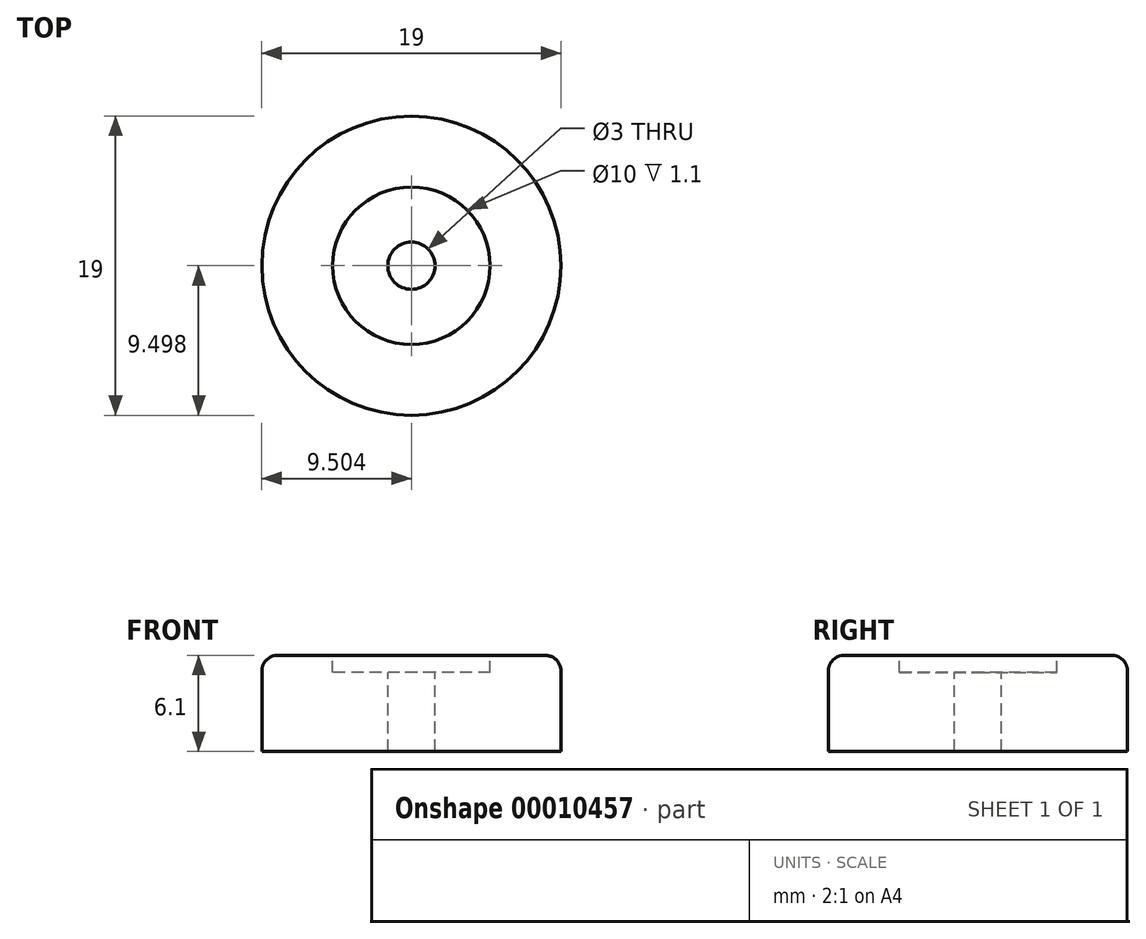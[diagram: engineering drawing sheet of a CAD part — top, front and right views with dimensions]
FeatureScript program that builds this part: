
annotation { "Feature Type Name" : "Feature", "Feature Type Description" : "" }
export const myFeature = defineFeature(function(context is Context, id is Id, definition is map)
    precondition{}
    {
        {
            var Q0;
            Q0=qCreatedBy(makeId("Top.planeOp"),FACE);
            var sketch = newSketch(context, id + "F0", { "sketchPlane" : qUnion([Q0])});
            skCircle(sketch, "E0", {"center": v(-57.53, -50.42) * mm, "radius": 9.5 * mm});
            skSolve(sketch);
        }
        {
            var Q0;
            Q0=makeQuery(id+"F0.imprint","IMPRINT",FACE,{"disambiguationData":[TD([[makeQuery(id+"F0.imprint","IMPRINT",EDGE,{"derivedFrom":sQuery(id+"F0.wireOp",EDGE,"E0")}),1.0]])]});
            extrude(context, id + "F1", {"entities" : qUnion([Q0]), "depth" : 6.1 * mm});
        }
        {
            var Q0;
            Q0=makeQuery(id+"F1.opExtrude","CAP_FACE",FACE,{"disambiguationData":[OSD([sQuery(id+"F0.wireOp",EDGE,"E0")])],"isStart":false});
            var sketch = newSketch(context, id + "F2", { "sketchPlane" : qUnion([Q0])});
            skCircle(sketch, "E1", {"center": v(-57.53, -50.42) * mm, "radius": 1.5 * mm});
            skSolve(sketch);
        }
        {
            var Q0;
            Q0 = qSketchRegion(id + "F2", true);
            extrude(context, id + "F3", {"entities" : qUnion([Q0]), "operationType" : NewBodyOperationType.REMOVE, "oppositeDirection" : true, "depth" : 6.1 * mm});
        }
        {
            var Q0;
            Q0=makeQuery(id+"F1.opExtrude","CAP_FACE",FACE,{"disambiguationData":[OSD([sQuery(id+"F0.wireOp",EDGE,"E0")])],"isStart":false});
            var sketch = newSketch(context, id + "F4", { "sketchPlane" : qUnion([Q0])});
            skCircle(sketch, "E2", {"center": v(-57.53, -50.42) * mm, "radius": 5 * mm});
            skSolve(sketch);
        }
        {
            var Q0;
            Q0=makeQuery(id+"F4.imprint","IMPRINT",FACE,{"disambiguationData":[TD([[makeQuery(id+"F4.imprint","IMPRINT",EDGE,{"derivedFrom":sQuery(id+"F4.wireOp",EDGE,"E2")}),1.0]])]});
            extrude(context, id + "F5", {"entities" : qUnion([Q0]), "operationType" : NewBodyOperationType.REMOVE, "oppositeDirection" : true, "depth" : 1.1 * mm});
        }
        {
            var Q0;
            Q0=makeQuery(id+"F1.opExtrude","CAP_EDGE",EDGE,{"disambiguationData":[OSD([sQuery(id+"F0.wireOp",EDGE,"E0")])],"isStart":false});
            fillet(context, id + "F6", {"entities" : qUnion([Q0]), "radius" : 1 * mm, "tangentPropagation" : true, "allowEdgeOverflow" : false});
        }
    });
